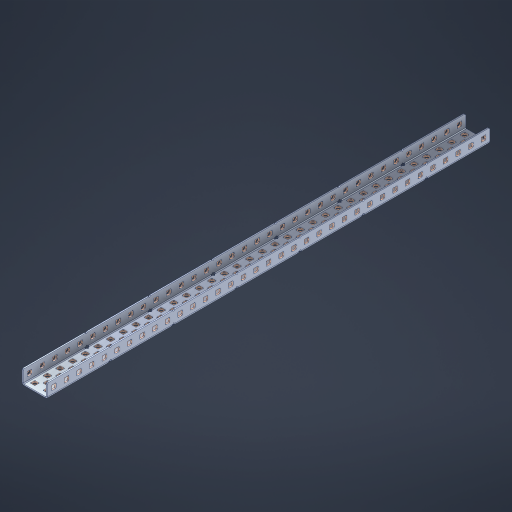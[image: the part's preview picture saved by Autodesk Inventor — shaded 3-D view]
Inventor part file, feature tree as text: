
AUTODESK INVENTOR PART (.ipt)
format: ipt  version: 2023 (Build 270158000, 158)  size: 2,065,408 bytes
history: native  units: in
note: dims shown in document units (in); Inventor stores cm internally (conversion verified against a paired STEP export)
features: other x181, extrude x172, sheet_metal_op x11, sketch x10, pattern_linear x2, mirror x1, chamfer x1
ambient origin geometry x8: Origin, YZ Plane, XZ Plane, XY Plane, X Axis, Y Axis, Z Axis, Center Point
bodies: Solid1 (feature_tree), Body (feature_tree)
feature tree (378):
  sheet_metal_op  "Flanges"
  other  "Flange Pattern Plane"
  other  "Flange Pattern Sketch"
  sheet_metal_op  "Flange Pattern"
  sheet_metal_op  "Body Pattern"
  pattern_linear  "Center Pattern"  Spacing1=0.0469in  [1 undecoded]
  other  "Arc Length"
  mirror  "Notch Mirror"
  pattern_linear  "Notch Pattern"  Spacing1=0.182in  [1 undecoded]
  chamfer  "End Chamfer"
  extrude  "Half Cut"  Depth=0.02in
  sketch  "Sketch1"  dims[d0=1.0in]
  other  "Plate1"
  sketch  "Sketch2"  dims[d1=17.5in]
  other  "Plate2"
  sheet_metal_op  "Bend1"
  sheet_metal_op  "Corner1"
  sketch  "Sketch3"  dims[d2=0.0469in]
  sketch  "Sketch7"  dims[d3=0.0469in]
  other  "Srf1"
  other  "Srf2"
  sketch  "Sketch8"  dims[d4=0.0234in]
  sketch  "Sketch9"  dims[d5=0.0938in]
  other  "Srf91"
  sheet_metal_op  "Body Pattern Sketch"
  other  "Srf92"
  sketch  "Sketch13"  dims[d6=0.0469in]
  sketch  "Sketch14"  dims[d7=0.5in d8=90.0deg d9=0.0312in]
  sketch  "Sketch15"  dims[d10=0.1875in]
  sketch  "Sketch16"  dims[d11=0.0469in d12=0.0469in d16=0.182in d17=0.02in d18=0.0469in d19=0.0in d20=0.25in d21=0.25in d38=13.7795in d40=0.5in d41=0.7874in d43=1.0in d46=0.172in d47=1.0in d48=0.0in d49=0.182in d50=0.02in d51=0.25in d52=0.25in d53=0.0469in d54=0.0in d55=0.172in d56=1.0in d57=0.0in d58=0.25in d60=13.7795in d62=0.5in d63=0.7874in d65=0.5in d85=0.1227in d86=0.1659in d88=0.04in d89=0.0469in d90=0.0in d91=0.04in d92=0.0491in d95=2.5in d96=0.04in d97=0.25in d98=45.0deg d99=0.25in d100=0.5in d101=0.0in d102=2.497in d106=0.182in d107=0.02in d108=0.5in d109=0.5in d110=0.0469in d111=0.0in d112=0.172in d113=0.5in d114=0.0in d117=0.5in d118=0.5in d119=0.5in]
  other  "Srf786"
  other  "Srf823"
  other  "Srf824"
  other  "Srf825"
  other  "Srf826"
  other  "Srf827"
  other  "Srf828"
  other  "Srf829"
  other  "Srf856"
  other  "Srf857"
  other  "Srf858"
  other  "Srf859"
  other  "Srf860"
  other  "Srf861"
  other  "Srf862"
  other  "Srf889"
  other  "Srf890"
  other  "Srf891"
  other  "Srf892"
  other  "Srf893"
  other  "Srf894"
  other  "Srf895"
  other  "Srf896"
  other  "Srf922"
  other  "Srf923"
  other  "Srf924"
  other  "Srf925"
  other  "Srf926"
  other  "Srf959"
  other  "Srf960"
  other  "Srf961"
  other  "Srf962"
  other  "Srf963"
  other  "Srf996"
  other  "Srf997"
  other  "Srf998"
  other  "Srf999"
  other  "Srf1000"
  other  "Srf1143"
  other  "Srf1144"
  other  "Srf1145"
  other  "Srf1146"
  other  "Srf1147"
  other  "Srf1148"
  other  "Srf1149"
  other  "Srf1150"
  other  "Srf1151"
  other  "Srf1152"
  other  "Srf1153"
  other  "Srf1154"
  other  "Srf1155"
  other  "Srf1156"
  other  "Srf1157"
  other  "Srf1158"
  other  "Srf1159"
  other  "Srf1160"
  other  "Srf1161"
  other  "Srf1162"
  other  "Srf1163"
  other  "Srf1164"
  other  "Srf1165"
  other  "Srf1166"
  other  "Srf1167"
  other  "Srf1168"
  other  "Srf1169"
  other  "Srf1170"
  other  "Srf1171"
  other  "Srf1172"
  other  "Srf1173"
  other  "Srf1174"
  other  "Srf1175"
  other  "Srf1176"
  other  "Srf1177"
  other  "Srf1178"
  other  "Srf1179"
  other  "Srf1180"
  other  "Srf1181"
  other  "Srf1182"
  other  "Srf1183"
  other  "Srf1184"
  other  "Srf1185"
  other  "Srf1186"
  other  "Srf1187"
  other  "Srf1188"
  other  "Srf1189"
  other  "Srf1190"
  other  "Srf1191"
  other  "Srf1192"
  other  "Srf1193"
  other  "Srf1194"
  other  "Srf1195"
  other  "Srf1196"
  other  "Srf1197"
  other  "Srf1198"
  other  "Srf1199"
  other  "Srf1200"
  other  "Srf1201"
  other  "Srf1202"
  other  "Srf1203"
  other  "Srf1204"
  other  "Srf1205"
  other  "Srf1206"
  other  "Srf1207"
  other  "Srf1208"
  other  "Srf1209"
  other  "Srf1210"
  other  "Srf1211"
  other  "Srf1212"
  other  "Srf1213"
  other  "Srf1214"
  other  "Srf1215"
  other  "Srf1216"
  other  "Srf1217"
  other  "Srf1218"
  other  "Srf1219"
  other  "Srf1220"
  other  "Srf1221"
  other  "Srf1222"
  other  "Srf1223"
  other  "Srf1224"
  other  "Srf1225"
  other  "Srf1226"
  other  "Srf1227"
  other  "Srf1228"
  other  "Srf1229"
  other  "Srf1230"
  other  "Srf1231"
  other  "Srf1232"
  other  "Srf1233"
  other  "Srf1234"
  other  "Srf1235"
  other  "Srf1236"
  other  "Srf1237"
  other  "Srf1238"
  other  "Srf1239"
  other  "Srf1240"
  other  "Srf1241"
  other  "Srf1242"
  other  "Srf1243"
  other  "Srf1244"
  other  "Srf1245"
  other  "Srf1246"
  other  "Srf1247"
  other  "Srf1248"
  other  "Srf1249"
  other  "Srf1250"
  other  "Srf1251"
  other  "Srf1252"
  other  "Srf1253"
  other  "Srf1254"
  other  "Srf1255"
  other  "Srf1256"
  other  "Srf1257"
  other  "Srf1258"
  other  "Srf1259"
  other  "Srf1260"
  other  "Srf1261"
  other  "Srf1262"
  other  "Srf1263"
  other  "Srf1264"
  other  "Srf1265"
  other  "Srf1266"
  other  "Srf1267"
  other  "Srf1268"
  other  "Srf1269"
  other  "Srf1270"
  other  "Srf1271"
  other  "Srf1272"
  other  "Srf1273"
  other  "Srf1274"
  sheet_metal_op  "Flange Stamp"
  sheet_metal_op  "Flange Circle"
  sheet_metal_op  "Body Stamp"
  sheet_metal_op  "Body Circle"
  other  "Center Stamp"
  other  "Center Circle"
  sheet_metal_op  "Notch"
  extrude  "ExtrusionSrf2"  Depth=0.0469in
  extrude  "ExtrusionSrf92"  TaperAngle=0.0deg  [1 undecoded]
  extrude  "ExtrusionSrf823"  Depth=0.5in
  extrude  "ExtrusionSrf824"  Depth=0.5in
  extrude  "ExtrusionSrf825"  Depth=0.5in
  extrude  "ExtrusionSrf826"  Depth=0.5in
  extrude  "ExtrusionSrf827"  Depth=1.0in TaperAngle=0.0deg
  extrude  "ExtrusionSrf828"  Depth=0.5in
  extrude  "ExtrusionSrf829"  Depth=0.02in
  extrude  "ExtrusionSrf856"  Depth=0.5in
  extrude  "ExtrusionSrf857"  Depth=0.5in
  extrude  "ExtrusionSrf858"  Depth=0.0469in
  extrude  "ExtrusionSrf859"  TaperAngle=0.0deg  [1 undecoded]
  extrude  "ExtrusionSrf860"  Depth=0.5in
  extrude  "ExtrusionSrf861"  Depth=1.0in TaperAngle=0.0deg
  extrude  "ExtrusionSrf862"  Depth=0.5in
  extrude  "ExtrusionSrf889"  Depth=0.5in
  extrude  "ExtrusionSrf890"  Depth=0.5in
  extrude  "ExtrusionSrf891"  Depth=0.5in
  extrude  "ExtrusionSrf892"  Depth=0.5in
  extrude  "ExtrusionSrf893"  Depth=0.5in
  extrude  "ExtrusionSrf894"  Depth=0.0469in
  extrude  "ExtrusionSrf895"  TaperAngle=0.0deg  [1 undecoded]
  extrude  "ExtrusionSrf896"  Depth=0.5in
  extrude  "ExtrusionSrf922"  Depth=0.5in
  extrude  "ExtrusionSrf923"  Depth=2.5in
  extrude  "ExtrusionSrf924"  Depth=0.5in TaperAngle=45.0deg
  extrude  "ExtrusionSrf925"  Depth=0.5in
  extrude  "ExtrusionSrf926"  Depth=0.5in TaperAngle=0.0deg
  extrude  "ExtrusionSrf959"  Depth=0.5in
  extrude  "ExtrusionSrf960"  Depth=0.5in
  extrude  "ExtrusionSrf961"  Depth=0.02in
  extrude  "ExtrusionSrf962"  Depth=0.5in
  extrude  "ExtrusionSrf963"  Depth=0.5in
  extrude  "ExtrusionSrf996"  Depth=0.0469in
  extrude  "ExtrusionSrf997"  TaperAngle=0.0deg  [1 undecoded]
  extrude  "ExtrusionSrf998"  Depth=0.5in
  extrude  "ExtrusionSrf999"  Depth=0.5in TaperAngle=0.0deg
  extrude  "ExtrusionSrf1000"  Depth=0.5in
  extrude  "ExtrusionSrf1143"  Depth=0.5in
  extrude  "ExtrusionSrf1144"  Depth=0.5in
  extrude  "ExtrusionSrf1145"  [1 undecoded]
  extrude  "ExtrusionSrf1146"  [1 undecoded]
  extrude  "ExtrusionSrf1147"  [1 undecoded]
  extrude  "ExtrusionSrf1148"  [1 undecoded]
  extrude  "ExtrusionSrf1149"  [1 undecoded]
  extrude  "ExtrusionSrf1150"  [1 undecoded]
  extrude  "ExtrusionSrf1151"  [1 undecoded]
  extrude  "ExtrusionSrf1152"  [1 undecoded]
  extrude  "ExtrusionSrf1153"  [1 undecoded]
  extrude  "ExtrusionSrf1154"  [1 undecoded]
  extrude  "ExtrusionSrf1155"  [1 undecoded]
  extrude  "ExtrusionSrf1156"  [1 undecoded]
  extrude  "ExtrusionSrf1157"  [1 undecoded]
  extrude  "ExtrusionSrf1158"  [1 undecoded]
  extrude  "ExtrusionSrf1159"  [1 undecoded]
  extrude  "ExtrusionSrf1160"  [1 undecoded]
  extrude  "ExtrusionSrf1161"  [1 undecoded]
  extrude  "ExtrusionSrf1162"  [1 undecoded]
  extrude  "ExtrusionSrf1163"  [1 undecoded]
  extrude  "ExtrusionSrf1164"  [1 undecoded]
  extrude  "ExtrusionSrf1165"  [1 undecoded]
  extrude  "ExtrusionSrf1166"  [1 undecoded]
  extrude  "ExtrusionSrf1167"  [1 undecoded]
  extrude  "ExtrusionSrf1168"  [1 undecoded]
  extrude  "ExtrusionSrf1169"  [1 undecoded]
  extrude  "ExtrusionSrf1170"  [1 undecoded]
  extrude  "ExtrusionSrf1171"  [1 undecoded]
  extrude  "ExtrusionSrf1172"  [1 undecoded]
  extrude  "ExtrusionSrf1173"  [1 undecoded]
  extrude  "ExtrusionSrf1174"  [1 undecoded]
  extrude  "ExtrusionSrf1175"  [1 undecoded]
  extrude  "ExtrusionSrf1176"  [1 undecoded]
  extrude  "ExtrusionSrf1177"  [1 undecoded]
  extrude  "ExtrusionSrf1178"  [1 undecoded]
  extrude  "ExtrusionSrf1179"  [1 undecoded]
  extrude  "ExtrusionSrf1180"  [1 undecoded]
  extrude  "ExtrusionSrf1181"  [1 undecoded]
  extrude  "ExtrusionSrf1182"  [1 undecoded]
  extrude  "ExtrusionSrf1183"  [1 undecoded]
  extrude  "ExtrusionSrf1184"  [1 undecoded]
  extrude  "ExtrusionSrf1185"  [1 undecoded]
  extrude  "ExtrusionSrf1186"  [1 undecoded]
  extrude  "ExtrusionSrf1187"  [1 undecoded]
  extrude  "ExtrusionSrf1188"  [1 undecoded]
  extrude  "ExtrusionSrf1189"  [1 undecoded]
  extrude  "ExtrusionSrf1190"  [1 undecoded]
  extrude  "ExtrusionSrf1191"  [1 undecoded]
  extrude  "ExtrusionSrf1192"  [1 undecoded]
  extrude  "ExtrusionSrf1193"  [1 undecoded]
  extrude  "ExtrusionSrf1194"  [1 undecoded]
  extrude  "ExtrusionSrf1195"  [1 undecoded]
  extrude  "ExtrusionSrf1196"  [1 undecoded]
  extrude  "ExtrusionSrf1197"  [1 undecoded]
  extrude  "ExtrusionSrf1198"  [1 undecoded]
  extrude  "ExtrusionSrf1199"  [1 undecoded]
  extrude  "ExtrusionSrf1200"  [1 undecoded]
  extrude  "ExtrusionSrf1201"  [1 undecoded]
  extrude  "ExtrusionSrf1202"  [1 undecoded]
  extrude  "ExtrusionSrf1203"  [1 undecoded]
  extrude  "ExtrusionSrf1204"  [1 undecoded]
  extrude  "ExtrusionSrf1205"  [1 undecoded]
  extrude  "ExtrusionSrf1206"  [1 undecoded]
  extrude  "ExtrusionSrf1207"  [1 undecoded]
  extrude  "ExtrusionSrf1208"  [1 undecoded]
  extrude  "ExtrusionSrf1209"  [1 undecoded]
  extrude  "ExtrusionSrf1210"  [1 undecoded]
  extrude  "ExtrusionSrf1211"  [1 undecoded]
  extrude  "ExtrusionSrf1212"  [1 undecoded]
  extrude  "ExtrusionSrf1213"  [1 undecoded]
  extrude  "ExtrusionSrf1214"  [1 undecoded]
  extrude  "ExtrusionSrf1215"  [1 undecoded]
  extrude  "ExtrusionSrf1216"  [1 undecoded]
  extrude  "ExtrusionSrf1217"  [1 undecoded]
  extrude  "ExtrusionSrf1218"  [1 undecoded]
  extrude  "ExtrusionSrf1219"  [1 undecoded]
  extrude  "ExtrusionSrf1220"  [1 undecoded]
  extrude  "ExtrusionSrf1221"  [1 undecoded]
  extrude  "ExtrusionSrf1222"  [1 undecoded]
  extrude  "ExtrusionSrf1223"  [1 undecoded]
  extrude  "ExtrusionSrf1224"  [1 undecoded]
  extrude  "ExtrusionSrf1225"  [1 undecoded]
  extrude  "ExtrusionSrf1226"  [1 undecoded]
  extrude  "ExtrusionSrf1227"  [1 undecoded]
  extrude  "ExtrusionSrf1228"  [1 undecoded]
  extrude  "ExtrusionSrf1229"  [1 undecoded]
  extrude  "ExtrusionSrf1230"  [1 undecoded]
  extrude  "ExtrusionSrf1231"  [1 undecoded]
  extrude  "ExtrusionSrf1232"  [1 undecoded]
  extrude  "ExtrusionSrf1233"  [1 undecoded]
  extrude  "ExtrusionSrf1234"  [1 undecoded]
  extrude  "ExtrusionSrf1235"  [1 undecoded]
  extrude  "ExtrusionSrf1236"  [1 undecoded]
  extrude  "ExtrusionSrf1237"  [1 undecoded]
  extrude  "ExtrusionSrf1238"  [1 undecoded]
  extrude  "ExtrusionSrf1239"  [1 undecoded]
  extrude  "ExtrusionSrf1240"  [1 undecoded]
  extrude  "ExtrusionSrf1241"  [1 undecoded]
  extrude  "ExtrusionSrf1242"  [1 undecoded]
  extrude  "ExtrusionSrf1243"  [1 undecoded]
  extrude  "ExtrusionSrf1244"  [1 undecoded]
  extrude  "ExtrusionSrf1245"  [1 undecoded]
  extrude  "ExtrusionSrf1246"  [1 undecoded]
  extrude  "ExtrusionSrf1247"  [1 undecoded]
  extrude  "ExtrusionSrf1248"  [1 undecoded]
  extrude  "ExtrusionSrf1249"  [1 undecoded]
  extrude  "ExtrusionSrf1250"  [1 undecoded]
  extrude  "ExtrusionSrf1251"  [1 undecoded]
  extrude  "ExtrusionSrf1252"  [1 undecoded]
  extrude  "ExtrusionSrf1253"  [1 undecoded]
  extrude  "ExtrusionSrf1254"  [1 undecoded]
  extrude  "ExtrusionSrf1255"  [1 undecoded]
  extrude  "ExtrusionSrf1256"  [1 undecoded]
  extrude  "ExtrusionSrf1257"  [1 undecoded]
  extrude  "ExtrusionSrf1258"  [1 undecoded]
  extrude  "ExtrusionSrf1259"  [1 undecoded]
  extrude  "ExtrusionSrf1260"  [1 undecoded]
  extrude  "ExtrusionSrf1261"  [1 undecoded]
  extrude  "ExtrusionSrf1262"  [1 undecoded]
  extrude  "ExtrusionSrf1263"  [1 undecoded]
  extrude  "ExtrusionSrf1264"  [1 undecoded]
  extrude  "ExtrusionSrf1265"  [1 undecoded]
  extrude  "ExtrusionSrf1266"  [1 undecoded]
  extrude  "ExtrusionSrf1267"  [1 undecoded]
  extrude  "ExtrusionSrf1268"  [1 undecoded]
  extrude  "ExtrusionSrf1269"  [1 undecoded]
  extrude  "ExtrusionSrf1270"  [1 undecoded]
  extrude  "ExtrusionSrf1271"  [1 undecoded]
  extrude  "ExtrusionSrf1272"  [1 undecoded]
  extrude  "ExtrusionSrf1273"  [1 undecoded]
  extrude  "ExtrusionSrf1274"  [1 undecoded]
note: 136 required parameter values undecoded (feature->parameter linkage not recoverable at this tier; creation-order binding heuristic only, values carry confidence <= 0.55)
